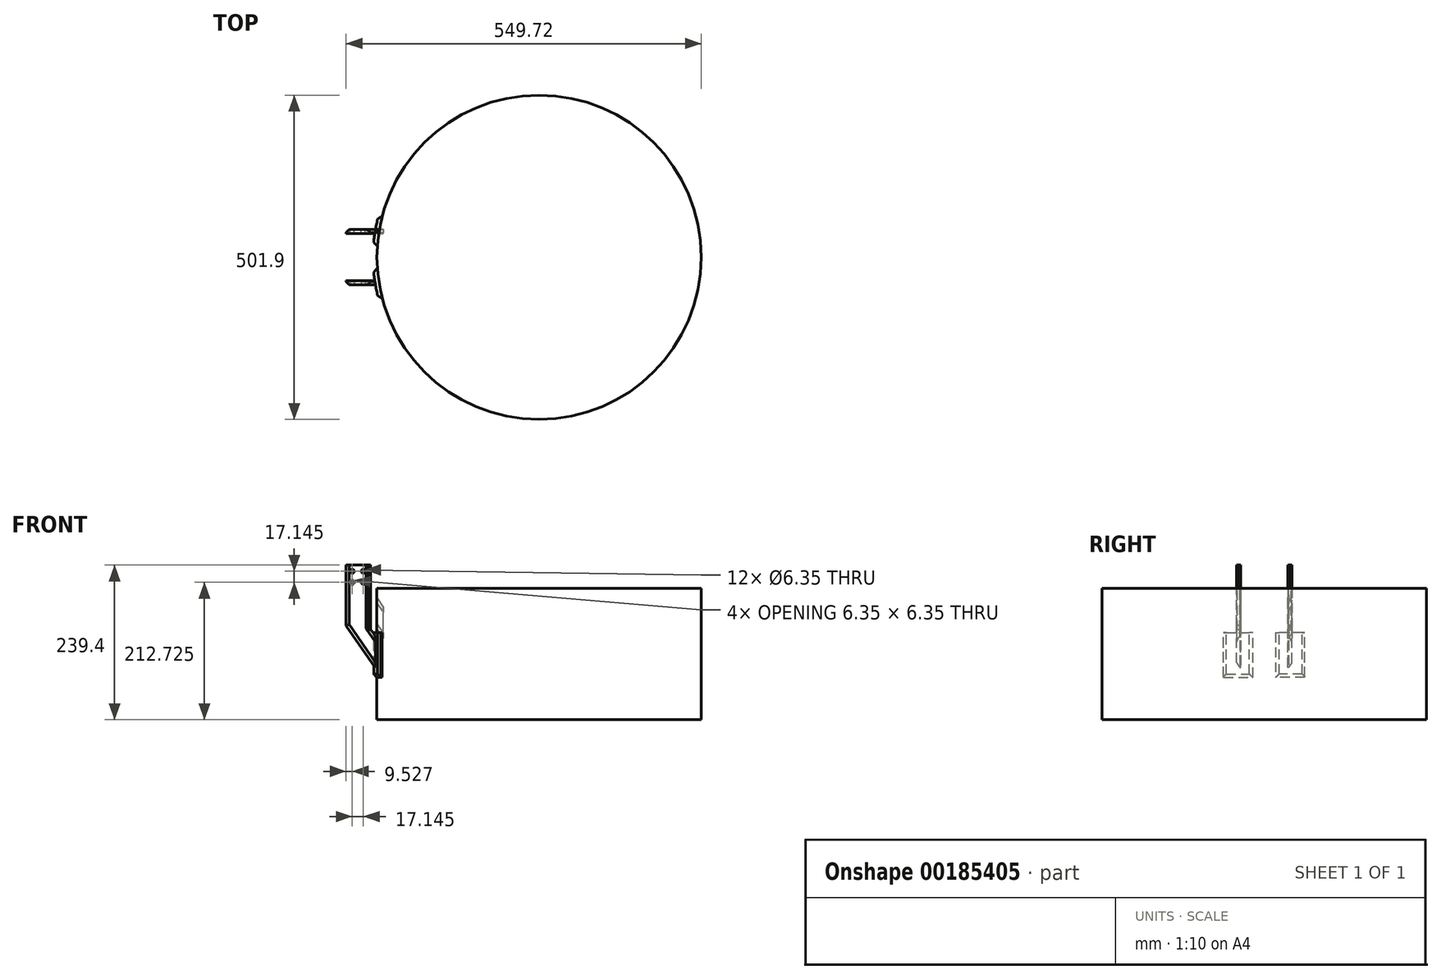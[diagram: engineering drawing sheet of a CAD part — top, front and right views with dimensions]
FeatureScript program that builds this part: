
annotation { "Feature Type Name" : "Feature", "Feature Type Description" : "" }
export const myFeature = defineFeature(function(context is Context, id is Id, definition is map)
    precondition{}
    {
        {
            var Q0;
            Q0=qCreatedBy(makeId("Top.planeOp"),FACE);
            var sketch = newSketch(context, id + "F0", { "sketchPlane" : qUnion([Q0])});
            skCircle(sketch, "E0", {"center": v(0, 0) * mm, "radius": 250.95 * mm});
            skLineSegment(sketch, "E1", {"start": v(0, 0) * mm, "end": v(0, 38.1) * mm});
            skLineSegment(sketch, "E2", {"start": v(0, 38.1) * mm, "end": v(0, 42.86) * mm});
            skLineSegment(sketch, "E3", {"start": v(0, 42.86) * mm, "end": v(-34.3, 42.86) * mm});
            skLineSegment(sketch, "E4", {"start": v(-34.3, 42.86) * mm, "end": v(-39.05, 42.86) * mm});
            skLineSegment(sketch, "E5", {"start": v(-39.05, 42.86) * mm, "end": v(-44.13, 42.86) * mm});
            skLineSegment(sketch, "E6", {"start": v(-44.13, 42.86) * mm, "end": v(-262.57, 42.86) * mm});
            skLineSegment(sketch, "E7", {"start": v(-262.57, 42.86) * mm, "end": v(-272.1, 42.86) * mm});
            skSolve(sketch);
        }
        {
            var Q0;
            Q0=sQuery(id+"F0.wireOp",EDGE,"E6");
            cPlane(context, id + "F1", {"entities" : qUnion([Q0]), "cplaneType" : CPlaneType.LINE_ANGLE, "offset" : 25.4 * mm, "angle" : 0 * degree, "width" : 152.4 * mm, "height" : 152.4 * mm});
        }
        {
            var Q0;
            Q0=qCreatedBy(id+"F1.planeOp",FACE);
            var sketch = newSketch(context, id + "F2", { "sketchPlane" : qUnion([Q0])});
            skLineSegment(sketch, "E8", {"start": v(-272.1, 0) * mm, "end": v(-272.1, 9.52) * mm});
            skLineSegment(sketch, "E9", {"start": v(-272.1, 9.52) * mm, "end": v(-289.24, 9.52) * mm});
            skLineSegment(sketch, "E10", {"start": v(-289.24, 9.52) * mm, "end": v(-289.24, 26.67) * mm});
            skLineSegment(sketch, "E11", {"start": v(-289.24, 26.67) * mm, "end": v(-272.1, 26.67) * mm});
            skSolve(sketch);
        }
        {
            var Q0;
            Q0=makeQuery(id+"F0.imprint","IMPRINT",FACE,{"disambiguationData":[TD([[makeQuery(id+"F0.imprint","IMPRINT",EDGE,{"derivedFrom":sQuery(id+"F0.wireOp",EDGE,"E0")}),1.0]])]});
            extrude(context, id + "F3", {"entities" : qUnion([Q0]), "oppositeDirection" : true, "depth" : 203.2 * mm});
        }
        {
            var Q0;
            Q0=qCreatedBy(id+"F1.planeOp",FACE);
            var sketch = newSketch(context, id + "F4", { "sketchPlane" : qUnion([Q0])});
            skLineSegment(sketch, "E12", {"start": v(-289.24, 26.67) * mm, "end": v(-289.24, 36.2) * mm});
            skLineSegment(sketch, "E13", {"start": v(-289.24, 36.2) * mm, "end": v(-298.77, 36.2) * mm});
            skLineSegment(sketch, "E14.bottom", {"start": v(-298.77, 36.2) * mm, "end": v(-260.67, 36.2) * mm});
            skLineSegment(sketch, "E14.left", {"start": v(-298.77, 36.2) * mm, "end": v(-298.77, 6) * mm});
            skLineSegment(sketch, "E14.right", {"start": v(-260.67, 36.2) * mm, "end": v(-260.67, 0) * mm});
            skLineSegment(sketch, "E15", {"start": v(-298.77, 6) * mm, "end": v(-241.15, -77.67) * mm});
            skLineSegment(sketch, "E16", {"start": v(-241.15, -77.67) * mm, "end": v(-241.15, -28.35) * mm});
            skLineSegment(sketch, "E17", {"start": v(-241.15, -28.35) * mm, "end": v(-260.67, 0) * mm});
            skLineSegment(sketch, "E18", {"start": v(-250.9, -14.17) * mm, "end": v(-250.9, -63.5) * mm});
            skLineSegment(sketch, "E19", {"start": v(-298.77, 6) * mm, "end": v(-298.77, -57.5) * mm});
            skLineSegment(sketch, "E20", {"start": v(-260.67, 0) * mm, "end": v(-260.67, -63.5) * mm});
            skLineSegment(sketch, "E21", {"start": v(-298.77, -57.5) * mm, "end": v(-241.15, -141.17) * mm});
            skLineSegment(sketch, "E22", {"start": v(-260.67, -63.5) * mm, "end": v(-222.14, -119.46) * mm});
            skLineSegment(sketch, "E23", {"start": v(-241.15, -141.17) * mm, "end": v(-241.4, -91.48) * mm});
            skSolve(sketch);
        }
        {
            var Q0;
            {var subQ3=sQuery(id+"F4.wireOp",EDGE,"E14.left");Q0=makeQuery(id+"F4.imprint","IMPRINT",FACE,{"disambiguationData":[TD([[makeQuery(id+"F4.imprint","IMPRINT",EDGE,{"derivedFrom":subQ3}),1.0]])]});}
            var Q1;
            {var subQ0=sQuery(id+"F4.wireOp",EDGE,"E16");Q1=makeQuery(id+"F4.imprint","IMPRINT",FACE,{"disambiguationData":[TD([[makeQuery(id+"F4.imprint","IMPRINT",EDGE,{"derivedFrom":subQ0}),1.0]])]});}
            var Q2;
            {var subQ5=sQuery(id+"F4.wireOp",EDGE,"E19");Q2=makeQuery(id+"F4.imprint","IMPRINT",FACE,{"disambiguationData":[TD([[makeQuery(id+"F4.imprint","IMPRINT",EDGE,{"derivedFrom":subQ5}),1.0]])]});}
            extrude(context, id + "F5", {"entities" : qUnion([Q0, Q1, Q2]), "depth" : 6.35 * mm});
        }
        {
            var Q0;
            Q0=makeQuery(id+"F3.opExtrude","SWEPT_BODY",BODY,{"disambiguationData":[OSD([sQuery(id+"F0.wireOp",EDGE,"E0")])]});
            var Q1;
            Q1=makeQuery(id+"F5.opExtrude","SWEPT_BODY",BODY,{"disambiguationData":[OSD([sQuery(id+"F4.wireOp",EDGE,"E14.bottom"),sQuery(id+"F4.wireOp",EDGE,"E14.left"),sQuery(id+"F4.wireOp",EDGE,"E14.right"),sQuery(id+"F4.wireOp",EDGE,"E15"),sQuery(id+"F4.wireOp",EDGE,"E17"),sQuery(id+"F4.wireOp",EDGE,"E18")])]});
            booleanBodies(context, id + "F6", {"operationType" : BooleanOperationType.INTERSECTION, "tools" : qUnion([Q0, Q1]), "keepTools" : true});
        }
        {
            var Q0;
            Q0=makeQuery(id+"F3.opExtrude","SWEPT_BODY",BODY,{"disambiguationData":[OSD([sQuery(id+"F0.wireOp",EDGE,"E0")])]});
            var Q1;
            Q1=makeQuery(id+"F6.opBoolean","INTERSECT",BODY,{"derivedFrom":[makeQuery(id+"F3.opExtrude","SWEPT_BODY",BODY,{"disambiguationData":[OSD([sQuery(id+"F0.wireOp",EDGE,"E0")])]}),makeQuery(id+"F5.opExtrude","SWEPT_BODY",BODY,{"disambiguationData":[OSD([sQuery(id+"F4.wireOp",EDGE,"E14.bottom"),sQuery(id+"F4.wireOp",EDGE,"E14.left"),sQuery(id+"F4.wireOp",EDGE,"E14.right"),sQuery(id+"F4.wireOp",EDGE,"E15"),sQuery(id+"F4.wireOp",EDGE,"E16"),sQuery(id+"F4.wireOp",EDGE,"E17")])]})]});
            booleanBodies(context, id + "F7", {"operationType" : BooleanOperationType.INTERSECTION, "tools" : qUnion([Q0, Q1]), "keepTools" : true});
        }
        {
            var Q0;
            {var subQ0=makeQuery(id+"F3.opExtrude","SWEPT_BODY",BODY,{"disambiguationData":[OSD([sQuery(id+"F0.wireOp",EDGE,"E0")])]});Q0=makeQuery(id+"F7.opBoolean","INTERSECT",BODY,{"derivedFrom":[subQ0,makeQuery(id+"F6.opBoolean","INTERSECT",BODY,{"derivedFrom":[subQ0,makeQuery(id+"F5.opExtrude","SWEPT_BODY",BODY,{"disambiguationData":[OSD([sQuery(id+"F4.wireOp",EDGE,"E14.bottom"),sQuery(id+"F4.wireOp",EDGE,"E14.left"),sQuery(id+"F4.wireOp",EDGE,"E14.right"),sQuery(id+"F4.wireOp",EDGE,"E15"),sQuery(id+"F4.wireOp",EDGE,"E16"),sQuery(id+"F4.wireOp",EDGE,"E17")])]})]})]});}
            deleteBodies(context, id + "F8", {"entities" : qUnion([Q0])});
        }
        {
            var Q0;
            Q0=makeQuery(id+"F3.opExtrude","SWEPT_BODY",BODY,{"disambiguationData":[OSD([sQuery(id+"F0.wireOp",EDGE,"E0")])]});
            var Q1;
            Q1=makeQuery(id+"F6.opBoolean","INTERSECT",BODY,{"derivedFrom":[makeQuery(id+"F3.opExtrude","SWEPT_BODY",BODY,{"disambiguationData":[OSD([sQuery(id+"F0.wireOp",EDGE,"E0")])]}),makeQuery(id+"F5.opExtrude","SWEPT_BODY",BODY,{"disambiguationData":[OSD([sQuery(id+"F4.wireOp",EDGE,"E14.bottom"),sQuery(id+"F4.wireOp",EDGE,"E14.left"),sQuery(id+"F4.wireOp",EDGE,"E14.right"),sQuery(id+"F4.wireOp",EDGE,"E15"),sQuery(id+"F4.wireOp",EDGE,"E16"),sQuery(id+"F4.wireOp",EDGE,"E17")])]})]});
            booleanBodies(context, id + "F9", {"operationType" : BooleanOperationType.SUBTRACTION, "tools" : qUnion([Q0]), "targets" : qUnion([Q1]), "keepTools" : true});
        }
        {
            var Q0;
            Q0=makeQuery(id+"F3.opExtrude","CAP_FACE",FACE,{"disambiguationData":[OSD([sQuery(id+"F0.wireOp",EDGE,"E0")])],"isStart":true});
            var sketch = newSketch(context, id + "F10", { "sketchPlane" : qUnion([Q0])});
            skCircle(sketch, "E24", {"center": v(0, 0) * mm, "radius": 250.83 * mm});
            skCircle(sketch, "E25", {"center": v(0, -2.3) * mm, "radius": 257.18 * mm});
            skLineSegment(sketch, "E26", {"start": v(-248.8, 62.8) * mm, "end": v(-238.41, 62.8) * mm});
            skLineSegment(sketch, "E27", {"start": v(-238.41, 62.8) * mm, "end": v(-238.41, 17.44) * mm});
            skLineSegment(sketch, "E28", {"start": v(-238.41, 17.44) * mm, "end": v(-256.42, 17.44) * mm});
            skSolve(sketch);
        }
        {
            var Q0;
            {var subQ0=sQuery(id+"F10.wireOp",EDGE,"E26");var subQ1=sQuery(id+"F10.wireOp",EDGE,"E25");var subQ2=makeQuery(id+"F10.imprint","INTERSECT",VERTEX,{"derivedFrom":[subQ1,subQ0]});Q0=makeQuery(id+"F10.imprint","IMPRINT",FACE,{"disambiguationData":[TD([[makeQuery(id+"F10.imprint","IMPRINT",EDGE,{"disambiguationData":[TD([[subQ2,-1.0]])],"derivedFrom":subQ1}),1.0]])]});}
            extrude(context, id + "F11", {"entities" : qUnion([Q0]), "oppositeDirection" : true, "depth" : 137.7 * mm, "hasSecondDirection" : true, "secondDirectionOppositeDirection" : true, "secondDirectionDepth" : 68.54 * mm});
        }
        {
            var Q0;
            Q0=makeQuery(id+"F11.opExtrude","SWEPT_EDGE",EDGE,{"disambiguationData":[OSD([sQuery(id+"F10.wireOp",EDGE,"E25"),sQuery(id+"F10.wireOp",EDGE,"E28")])]});
            var Q1;
            Q1=makeQuery(id+"F11.opExtrude","CAP_EDGE",EDGE,{"disambiguationData":[OSD([sQuery(id+"F10.wireOp",EDGE,"E25")])],"isStart":false});
            var Q2;
            Q2=makeQuery(id+"F11.opExtrude","SWEPT_EDGE",EDGE,{"disambiguationData":[OSD([sQuery(id+"F10.wireOp",EDGE,"E25"),sQuery(id+"F10.wireOp",EDGE,"E26")])]});
            var Q3;
            {var subQ0=makeQuery(id+"F5.opExtrude","CAP_EDGE",EDGE,{"disambiguationData":[OSD([sQuery(id+"F4.wireOp",EDGE,"E15")])],"isStart":true});Q3=makeQuery(id+"FtOgQkS5nuITGMW_3.opBoolean","MERGE",EDGE,{"derivedFrom":[subQ0,makeQuery(id+"F6.opBoolean","COPY",EDGE,{"derivedFrom":subQ0})]});}
            var Q4;
            Q4=makeQuery(id+"F5.opExtrude","CAP_EDGE",EDGE,{"disambiguationData":[OSD([sQuery(id+"F4.wireOp",EDGE,"E14.left")])],"isStart":true});
            var Q5;
            Q5=makeQuery(id+"F5.opExtrude","CAP_EDGE",EDGE,{"disambiguationData":[OSD([sQuery(id+"F4.wireOp",EDGE,"E14.right")])],"isStart":true});
            var Q6;
            {var subQ0=makeQuery(id+"F5.opExtrude","CAP_EDGE",EDGE,{"disambiguationData":[OSD([sQuery(id+"F4.wireOp",EDGE,"E17")])],"isStart":true});Q6=makeQuery(id+"FtOgQkS5nuITGMW_3.opBoolean","MERGE",EDGE,{"derivedFrom":[subQ0,makeQuery(id+"F6.opBoolean","COPY",EDGE,{"derivedFrom":subQ0})]});}
            chamfer(context, id + "F12", {"entities" : qUnion([Q0, Q1, Q2, Q3, Q4, Q5, Q6]), "width" : 5.08 * mm, "tangentPropagation" : true});
        }
        {
            var Q0;
            Q0=makeQuery(id+"F11.opExtrude","SWEPT_BODY",BODY,{"disambiguationData":[OSD([sQuery(id+"F0.wireOp",EDGE,"E0"),sQuery(id+"F10.wireOp",EDGE,"E25"),sQuery(id+"F10.wireOp",EDGE,"E26"),sQuery(id+"F10.wireOp",EDGE,"E28")])]});
            var Q1;
            Q1=makeQuery(id+"F5.opExtrude","SWEPT_BODY",BODY,{"disambiguationData":[OSD([sQuery(id+"F4.wireOp",EDGE,"E14.bottom"),sQuery(id+"F4.wireOp",EDGE,"E14.left"),sQuery(id+"F4.wireOp",EDGE,"E14.right"),sQuery(id+"F4.wireOp",EDGE,"E19"),sQuery(id+"F4.wireOp",EDGE,"E20"),sQuery(id+"F4.wireOp",EDGE,"E21"),sQuery(id+"F4.wireOp",EDGE,"E22"),sQuery(id+"F4.wireOp",EDGE,"E23")])]});
            booleanBodies(context, id + "F13", {"operationType" : BooleanOperationType.UNION, "tools" : qUnion([Q0, Q1])});
        }
        {
            var Q0;
            {var subQ0=sQuery(id+"F4.wireOp",EDGE,"E21");Q0=makeQuery(id+"F13.opBoolean","SPLIT",EDGE,{"disambiguationData":[TD([makeQuery(id+"F11.opExtrude","SWEPT_FACE",FACE,{"disambiguationData":[OSD([sQuery(id+"F10.wireOp",EDGE,"E25")])]})])],"derivedFrom":makeQuery(id+"F5.opExtrude","CAP_EDGE",EDGE,{"disambiguationData":[OSD([subQ0])],"isStart":true})});}
            var Q1;
            {var subQ0=sQuery(id+"F4.wireOp",EDGE,"E20");var subQ1=sQuery(id+"F4.wireOp",EDGE,"E14.right");Q1=makeQuery(id+"F12.opChamfer","BLEND_EDGE",EDGE,{"blendedFrom":[makeQuery(id+"F5.opExtrude","CAP_EDGE",EDGE,{"disambiguationData":[OSD([subQ1,subQ0])],"isStart":true}),makeQuery(id+"F5.opExtrude","CAP_FACE",FACE,{"disambiguationData":[OSD([sQuery(id+"F4.wireOp",EDGE,"E14.bottom"),sQuery(id+"F4.wireOp",EDGE,"E14.left"),subQ1,sQuery(id+"F4.wireOp",EDGE,"E19"),subQ0,sQuery(id+"F4.wireOp",EDGE,"E21"),sQuery(id+"F4.wireOp",EDGE,"E22"),sQuery(id+"F4.wireOp",EDGE,"E23")])],"isStart":true})],"blendedInto":[makeQuery(id+"F5.opExtrude","CAP_FACE",FACE,{"disambiguationData":[OSD([sQuery(id+"F4.wireOp",EDGE,"E14.bottom"),sQuery(id+"F4.wireOp",EDGE,"E14.left"),subQ1,sQuery(id+"F4.wireOp",EDGE,"E19"),subQ0,sQuery(id+"F4.wireOp",EDGE,"E21"),sQuery(id+"F4.wireOp",EDGE,"E22"),sQuery(id+"F4.wireOp",EDGE,"E23")])],"isStart":true})]});}
            var Q2;
            {var subQ0=sQuery(id+"F4.wireOp",EDGE,"E22");Q2=makeQuery(id+"F13.opBoolean","SPLIT",EDGE,{"disambiguationData":[TD([makeQuery(id+"F11.opExtrude","SWEPT_FACE",FACE,{"disambiguationData":[OSD([sQuery(id+"F10.wireOp",EDGE,"E25")])]})])],"derivedFrom":makeQuery(id+"F5.opExtrude","CAP_EDGE",EDGE,{"disambiguationData":[OSD([subQ0])],"isStart":true})});}
            chamfer(context, id + "F14", {"entities" : qUnion([Q0, Q1, Q2]), "width" : 5.08 * mm, "tangentPropagation" : true});
        }
        {
            var Q0;
            Q0=sQuery(id+"F2.wireOp",VERTEX,"E9.start");
            var Q1;
            Q1=sQuery(id+"F2.wireOp",VERTEX,"E10.start");
            var Q2;
            Q2=sQuery(id+"F4.wireOp",VERTEX,"E12.start");
            var Q3;
            Q3=sQuery(id+"F2.wireOp",VERTEX,"E11.end");
            var Q4;
            Q4=makeQuery(id+"F11.opExtrude","SWEPT_BODY",BODY,{"disambiguationData":[OSD([sQuery(id+"F0.wireOp",EDGE,"E0"),sQuery(id+"F10.wireOp",EDGE,"E25"),sQuery(id+"F10.wireOp",EDGE,"E26"),sQuery(id+"F10.wireOp",EDGE,"E28")])]});
            hole(context, id + "F15", {"style" : HoleStyle.SIMPLE, "endStyle" : HoleEndStyle.THROUGH, "oppositeDirection" : true, "holeDiameter" : 6.35 * mm, "locations" : qUnion([Q0, Q1, Q2, Q3]), "scope" : qUnion([Q4]), "isTappedThrough" : true});
        }
        {
            var Q0;
            Q0=makeQuery(id+"F3.opExtrude","SWEPT_BODY",BODY,{"disambiguationData":[OSD([sQuery(id+"F0.wireOp",EDGE,"E0")])]});
            var Q1;
            Q1=makeQuery(id+"F11.opExtrude","SWEPT_BODY",BODY,{"disambiguationData":[OSD([sQuery(id+"F0.wireOp",EDGE,"E0"),sQuery(id+"F10.wireOp",EDGE,"E25"),sQuery(id+"F10.wireOp",EDGE,"E26"),sQuery(id+"F10.wireOp",EDGE,"E28")])]});
            booleanBodies(context, id + "F16", {"operationType" : BooleanOperationType.SUBTRACTION, "tools" : qUnion([Q0]), "targets" : qUnion([Q1]), "keepTools" : true});
        }
        {
            var Q0;
            {var subQ5=sQuery(id+"F10.wireOp",EDGE,"E27");Q0=makeQuery(id+"F10.imprint","IMPRINT",FACE,{"disambiguationData":[TD([[makeQuery(id+"F10.imprint","IMPRINT",EDGE,{"derivedFrom":subQ5}),1.0]])]});}
            var sketch = newSketch(context, id + "F17", { "sketchPlane" : qUnion([Q0])});
            skLineSegment(sketch, "E29", {"start": v(0, 0) * mm, "end": v(-377.96, 0) * mm});
            skSolve(sketch);
        }
        {
            var Q0;
            Q0=sQuery(id+"F17.wireOp",EDGE,"E29");
            cPlane(context, id + "F18", {"entities" : qUnion([Q0]), "cplaneType" : CPlaneType.LINE_ANGLE, "offset" : 25.4 * mm, "angle" : 0 * degree, "width" : 152.4 * mm, "height" : 152.4 * mm});
        }
        {
            var Q0;
            Q0=makeQuery(id+"F11.opExtrude","SWEPT_BODY",BODY,{"disambiguationData":[OSD([sQuery(id+"F0.wireOp",EDGE,"E0"),sQuery(id+"F10.wireOp",EDGE,"E25"),sQuery(id+"F10.wireOp",EDGE,"E26"),sQuery(id+"F10.wireOp",EDGE,"E28")])]});
            var Q1;
            Q1=qCreatedBy(id+"F18.planeOp",FACE);
            mirror(context, id + "F19", {"entities" : qUnion([Q0]), "mirrorPlane" : qUnion([Q1])});
        }
        {
            var Q0;
            Q0=makeQuery(id+"F11.opExtrude","SWEPT_BODY",BODY,{"disambiguationData":[OSD([sQuery(id+"F0.wireOp",EDGE,"E0"),sQuery(id+"F10.wireOp",EDGE,"E25"),sQuery(id+"F10.wireOp",EDGE,"E26"),sQuery(id+"F10.wireOp",EDGE,"E28")])]});
            transform(context, id + "F20", {"entities" : qUnion([Q0]), "transformType" : TransformType.TRANSLATION_3D, "dx" : 0 * mm, "dy" : 0 * mm, "dz" : 0 * mm, "makeCopy" : true});
        }
    });
